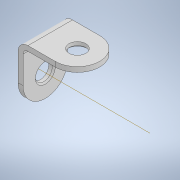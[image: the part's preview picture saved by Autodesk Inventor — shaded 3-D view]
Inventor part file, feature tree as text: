
AUTODESK INVENTOR PART (.ipt)
format: ipt  version: 2022 (Build 260153000, 153)  size: 148,992 bytes
history: native  units: mm
features: sketch x3, extrude x2, fillet x2, hole x1, plane x1, mirror x1, other x1, projected_geometry x1
ambient origin geometry x8: Origin, YZ Plane, XZ Plane, XY Plane, X Axis, Y Axis, Z Axis, Center Point
bodies: Solid1 (feature_tree)
feature tree (12):
  extrude  "Extrusion1"  Depth=12.0mm
  sketch  "Sketch2"  dims[d2=1.0mm d3=9.0mm d4=0.0mm]
  sketch  "Sketch5"  dims[d14=16.002mm d15=0.0mm d16=3.4mm d17=6.0mm d18=4.0mm d19=2.0mm d20=90.0deg d21=8.0mm d22=20.594885mm d23=2.0mm d24=1.0mm]
  hole  "Hole2"  [1 undecoded]
  extrude  "Extrusion3"  Depth=2.0mm
  plane  "Work Plane1"
  mirror  "Mirror1"
  other  "Work Axis1"
  fillet  "Fillet1"  Radius=1.0mm
  fillet  "Fillet2"  [1 undecoded]
  sketch  "Sketch1"  dims[d0=12.0mm d1=12.0mm]
  projected_geometry  "Projected Loop1"
note: 2 required parameter values undecoded (feature->parameter linkage not recoverable at this tier; creation-order binding heuristic only, values carry confidence <= 0.55)
